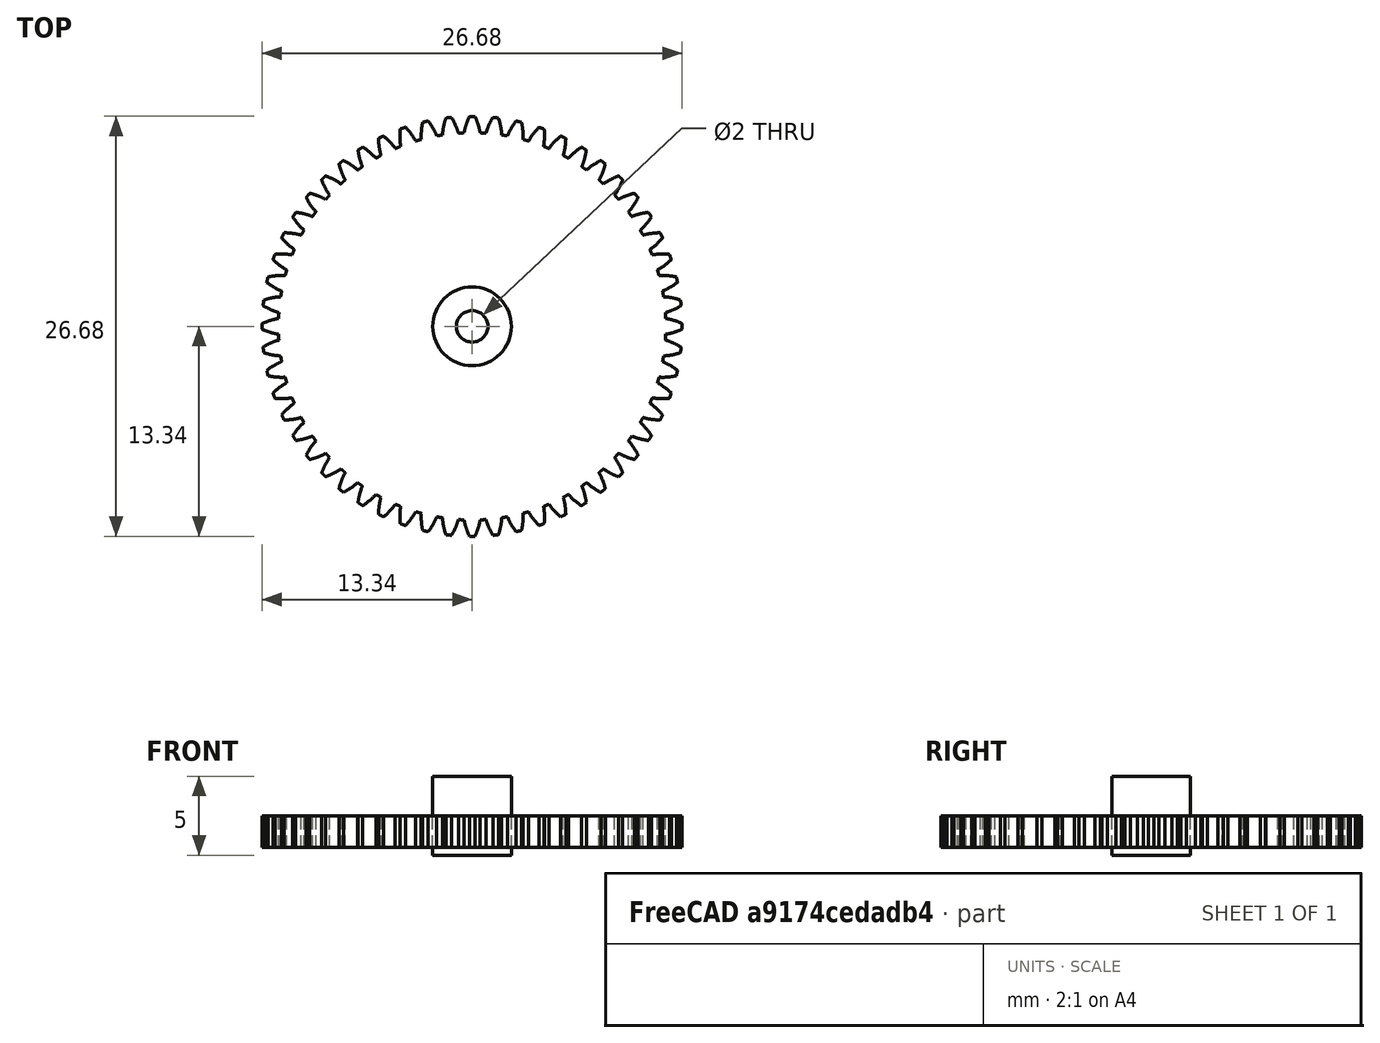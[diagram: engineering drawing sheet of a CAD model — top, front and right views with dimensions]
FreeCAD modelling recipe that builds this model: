
FCSTD DOCUMENT  (FreeCAD 0.19R21654 (Git))
Label: gear_from_picture
License: All rights reserved
LicenseURL: http://en.wikipedia.org/wiki/All_rights_reserved
objects: Part::Cylinder×2, Image::ImagePlane×1, Part::FeaturePython×1, Part::MultiFuse×1, Part::Cut×1, Part::Part2DObjectPython×1
note: 6 computed .brp shape members not serialized (recipe doc carries the construction recipe); baked Part::Feature solids carry a one-line shape summary decoded from their .brp

FEATURE [Image::ImagePlane] ImagePlane
  Placement = pos=(0,0,-22) rot=(0,0,1;0rad)
  XSize = 27
  YSize = 27
FEATURE [Part::Cylinder] Cylinder
  Angle = 360
  AttacherType = Attacher::AttachEngine3D
  Height = 5
  Placement = pos=(0,0,-0.5) rot=(0,0,1;0rad)
  Radius = 2.5
FEATURE [Part::Cylinder] Cylinder001
  Angle = 360
  AttacherType = Attacher::AttachEngine3D
  Height = 5
  Placement = pos=(0,0,-0.5) rot=(0,0,1;0rad)
  Radius = 1
FEATURE [Part::FeaturePython] InvoluteGear001  # WARN: FeaturePython — macro-defined, semantics opaque (R4)
  backlash = 0
  beta = 0
  clearance = 0.25
  double_helix = false
  dw = 25.76
  head = 0
  height = 2
  module = 0.46
  numpoints = 6
  pressure_angle = 20
  properties_from_tool = true
  reversed_backlash = false
  shift = 0
  simple = false
  teeth = 56
  transverse_pitch = 1.44513
  undercut = false
FEATURE [Part::MultiFuse] Fusion
  Shapes = -> [Cylinder,InvoluteGear001]
FEATURE [Part::Cut] Cut
  Base = -> Fusion
  Tool = -> Cylinder001
FEATURE [Part::Part2DObjectPython] Shape2DView  # Draft 2D object (typed FeaturePython)
  Base = -> Cut
  FaceNumbers = [4]
  HiddenLines = false
  InPlace = true
  Placement = pos=(0,0,-21.9) rot=(0,0,1;0rad)
  Projection = (0,0,1)
  ProjectionMode = 0
  SegmentLength = 0.05
  Tessellation = false
